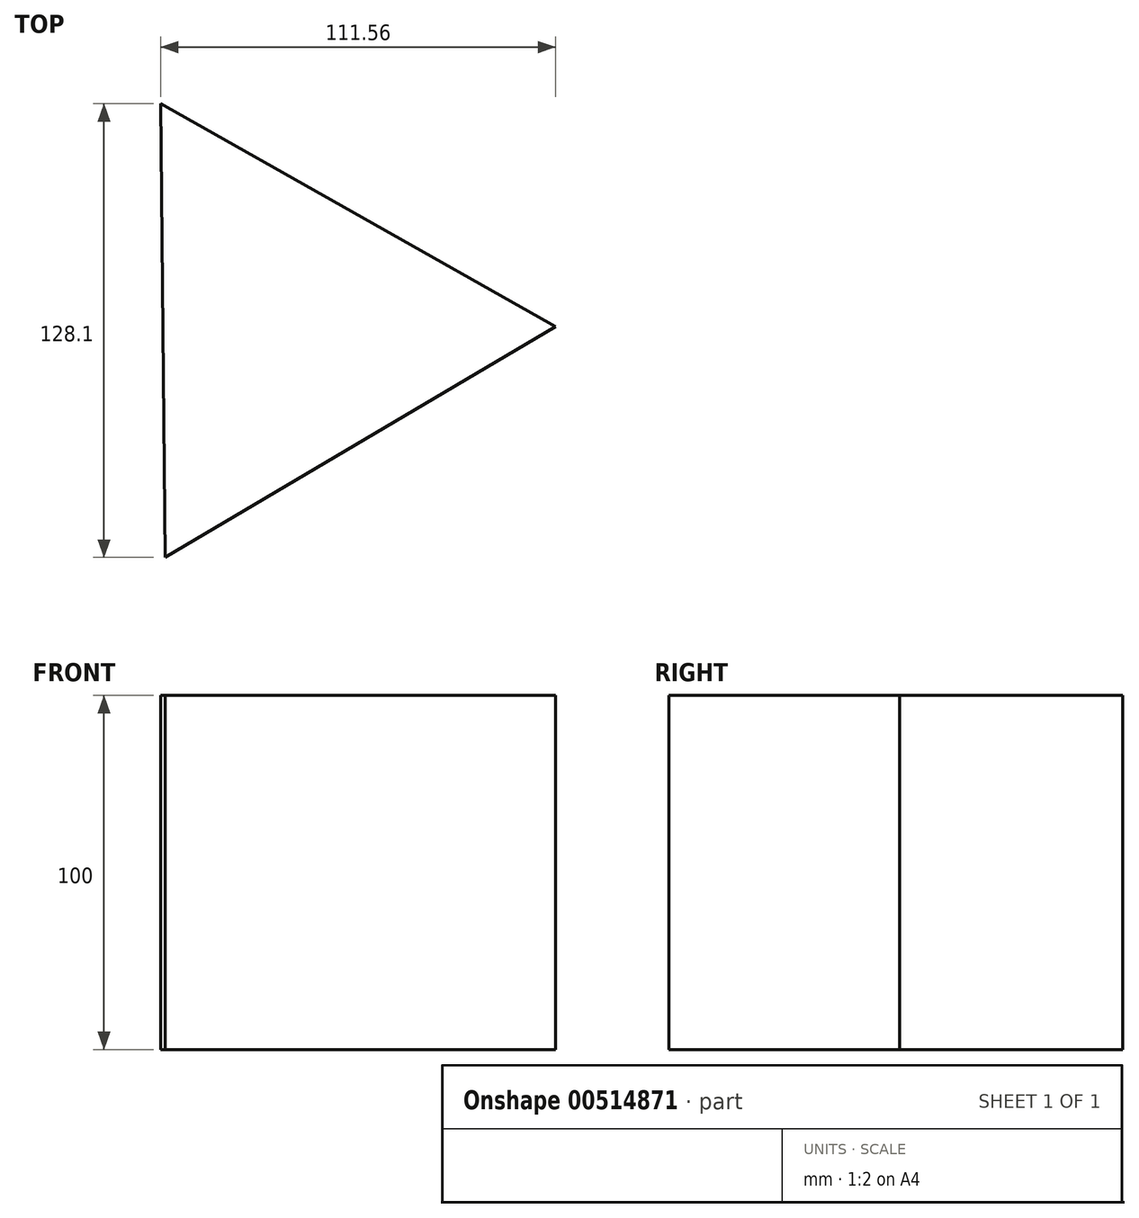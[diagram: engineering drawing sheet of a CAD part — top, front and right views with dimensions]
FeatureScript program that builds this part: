
annotation { "Feature Type Name" : "Feature", "Feature Type Description" : "" }
export const myFeature = defineFeature(function(context is Context, id is Id, definition is map)
    precondition{}
    {
        {
            var Q0;
            Q0=qCreatedBy(makeId("Top.planeOp"),FACE);
            var sketch = newSketch(context, id + "F0", { "sketchPlane" : qUnion([Q0])});
            skCircle(sketch, "E0.cCircle", {"center": v(0, 0) * mm, "radius": 73.96 * mm, "construction": true});
            skLineSegment(sketch, "E0.0", {"start": v(-37.6, 63.69) * mm, "end": v(73.96, 0.72) * mm});
            skLineSegment(sketch, "E0.1", {"start": v(73.96, 0.72) * mm, "end": v(-36.35, -64.4) * mm});
            skLineSegment(sketch, "E0.2", {"start": v(-36.35, -64.4) * mm, "end": v(-37.6, 63.69) * mm});
            skSolve(sketch);
        }
        {
            var Q0;
            Q0=makeQuery(id+"F0.imprint","IMPRINT",FACE,{"disambiguationData":[TD([[makeQuery(id+"F0.imprint","IMPRINT",EDGE,{"derivedFrom":sQuery(id+"F0.wireOp",EDGE,"E0.0")}),-1.0]])]});
            extrude(context, id + "F1", {"entities" : qUnion([Q0]), "depth" : 100 * mm, "offsetDistance" : 25.4 * mm});
        }
    });
